# Revit family: VLN_Aqua_B9320_BIM_NL
name_source: partatom
category: Plumbing Fixtures
revit_build: Autodesk Revit MEP 2016 (Build: 20161004_0715(x64)
units: mm (PartAtom-declared; Revit-internal decimal feet)

## family parameters
Always vertical = No
Cut with Voids When Loaded = No
OmniClass Number = 23.45.05.14.17
OmniClass Title = Showers
Part Type = Normal
Room Calculation Point = No
Round Connector Dimension = Use Diameter
Shared = No
Work Plane-Based = No

## types (1)
- B9320AA - AQUA BADSET MET HANDDOUCHE 3 FUNCTIES
    Accessories = www.idealstandardnederland.nl
    AssetType = Shower
    BIMobject category = Basins
    BOSUseNativeGeometries = 1
    BarCode = 3800861023586
    Brand = Venlo
    Brand url = http:\\www.idealstandardnederland.nl
    Category = Showers
    Color = Chroom
    ConnectionType = Sanitair
    CurrencyUnit = Euro
    CurrentRevision = 1.0
    Description = Venlo Aqua 100 badset. Handdouche 3 functies (Normaal / Champage / Massage). Draaibare handdouchehouder en douchesslang "Idealflex" 1250 mm. 8 l/min bij 3 bar.
    DurationUnit = jaar
    EAN code = https://3800861023586
    Edition number = 1
    ExpectedLife = 25
    Features = Badset. Handdouche 3 functies (Normaal / Champage / Massage). Draaibare handdouchehouder en douchesslang "Idealflex" 1250 mm. 8 l/min bij 3 bar.
    Finish = Chroom
    IFC Classification = Sanitary Terminal
    Installation instructions = http://www.idealstandardnederland.nl
    InstallationInstructions = http://www.idealstandardnederland.nl
    MainColor = Chroom
    Manufacturer name = Venlo
    Material = Messing
    Material main = Brassware
    Model = B9320AA
    ModelNumber = B9320AA
    ModelReference = B9320AA
    NBS Reference Code = 35-06-81
    NBS Reference Description = Shower Heads
    Name = AQUA BADSET MET HANDDOUCHE 3 FUNCTIES
    NettWeight = 0,60 KG
    Nominal height = 126
    Nominal width = 152
    NominalHeight = 272 mm
    NominalLength = 144 mm
    NominalWidth = 123 mm
    Product Guid = ee49de36-4b0a-4b42-bb53-68f04ddb857f
    Product SKU = B9320
    Product certification = http://www.idealstandardnederland.nl
    Product data url = https://bimobject.com
    Product family = Sanitary
    Product group = Shower fittings package
    Product name = AQUA BADSET MET HANDDOUCHE 3 FUNCTIES
    Product url = http://www.idealstandardnederland.nl
    QR code = http://bimobject.com
    Shape = Gesculptuurd
    Size = 123x144x272 mm
    SpareParts = www.idealstandardnederland.nl
    Technical description = http://www.idealstandardnederland.nl
    URL = http://www.idealstandardnederland.nl
    Uniclass 1.4 Code = L7214
    Uniclass 1.4 Description = Showers
    Uniclass 2.0 Code = PR-35-06-81
    Uniclass 2.0 Description = Shower Heads
    Uniclass 2015 Code = Pr_40_20_87_76
    Uniclass 2015 Name = Shower heads
    VolumeUnits = Liter
    WarrantyDescription = Fabrieksgarantie
    WarrantyDurationParts = 5
    WarrantyDurationUnit = jaar
    Weight Net (Kg) = 0.6

## geometry (parser evidence)
native form markers: Blend x4, Sweep x1
no freeform markers — native parametric forms only
